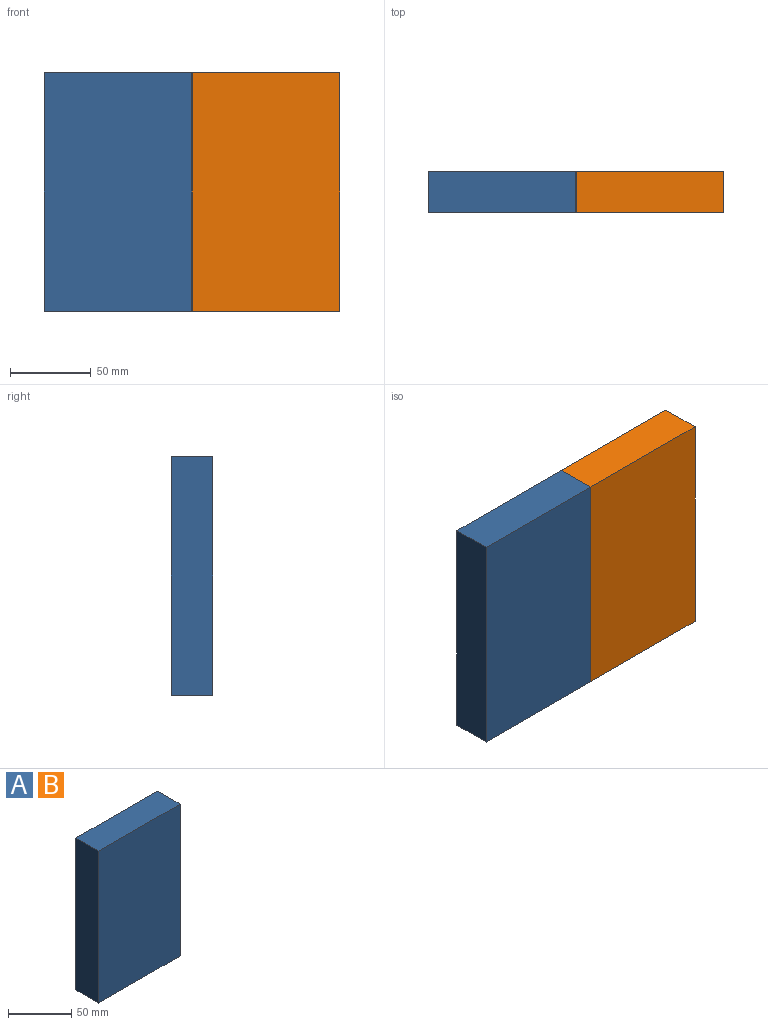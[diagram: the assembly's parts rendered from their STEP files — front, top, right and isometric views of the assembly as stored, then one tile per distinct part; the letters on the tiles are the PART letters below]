
ASSEMBLY  parts=2 mates=1
PART A: 6 faces, bbox 91.2x25.4x147.1 mm
  f0: plane 91.23x25.4mm, normal (0,0,-1), area 2317.2mm2, adj f1,f3,f4,f5
  f1: plane 147.11x25.4mm, normal (1,0,0), area 3736.5mm2, adj f0,f2,f4,f5
  f2: plane 91.23x25.4mm, normal (0,0,1), area 2317.2mm2, adj f1,f3,f4,f5
  f3: plane 147.11x25.4mm, normal (-1,0,0), area 3736.5mm2, adj f0,f2,f4,f5
  f4: plane 147.11x91.23mm, normal (0,-1,0), area 13420.3mm2, adj f0,f1,f2,f3
  f5: plane 147.11x91.23mm, normal (0,1,0), area 13420.3mm2, adj f0,f1,f2,f3
PART B: same geometry as A
PLACE A t=(0,12.7,-73.55)mm
PLACE B t=(91.23,12.7,-73.55)mm
MATE fastened A.f4 <-> B.f4  axis (0,-1,0) through (45.61,-12.7,0)mm
